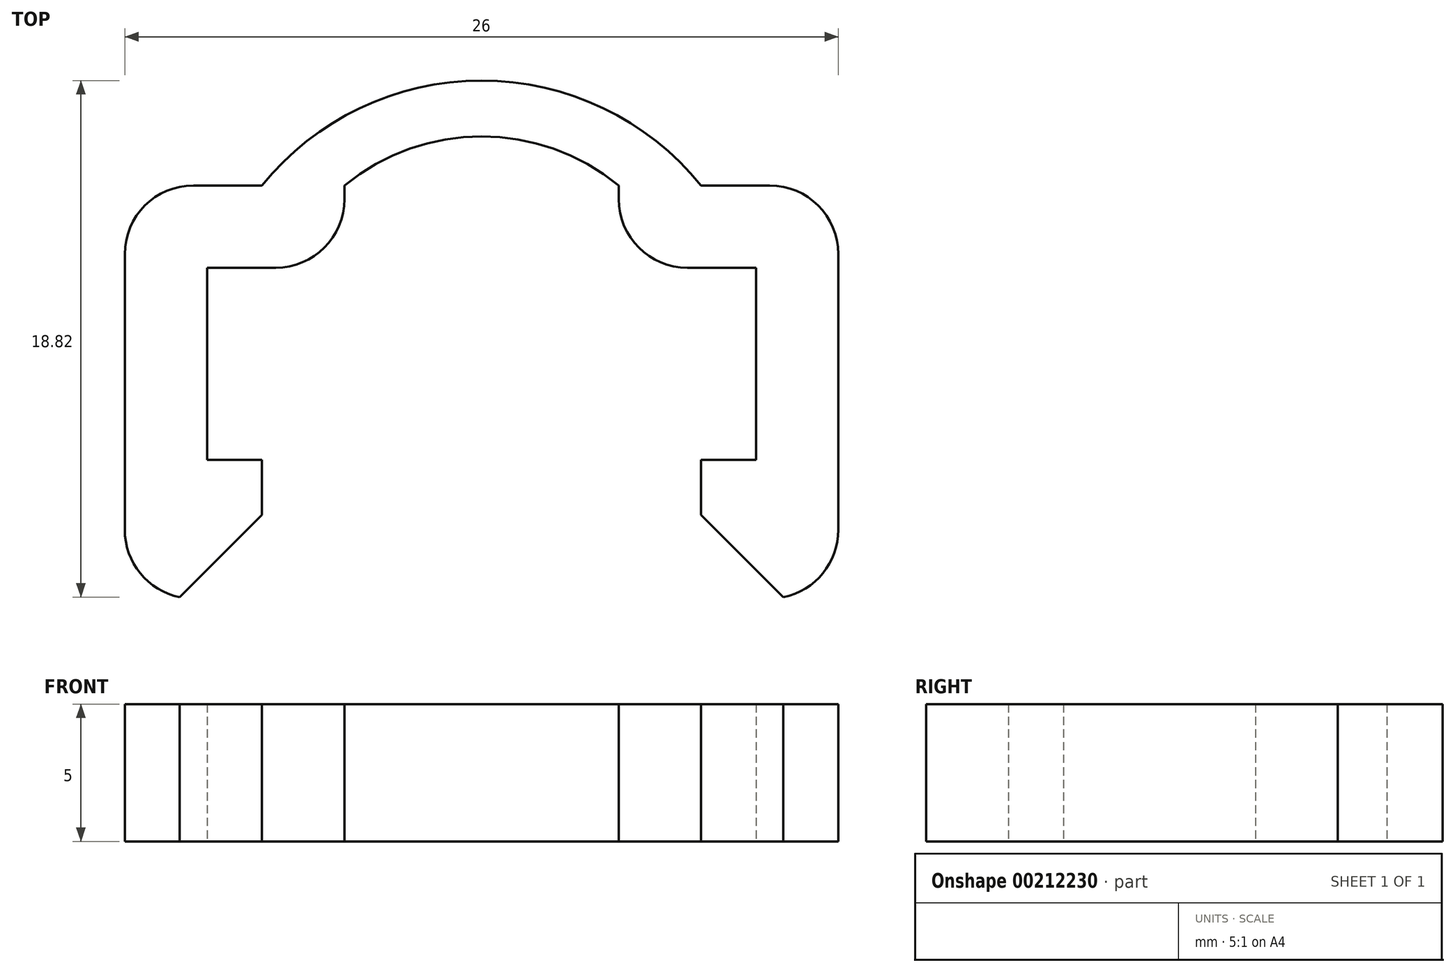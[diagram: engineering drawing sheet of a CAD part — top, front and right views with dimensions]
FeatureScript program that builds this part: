
annotation { "Feature Type Name" : "Feature", "Feature Type Description" : "" }
export const myFeature = defineFeature(function(context is Context, id is Id, definition is map)
    precondition{}
    {
        {
            var Q0;
            Q0=qCreatedBy(makeId("Top.planeOp"),FACE);
            var sketch = newSketch(context, id + "F0", { "sketchPlane" : qUnion([Q0])});
            skLineSegment(sketch, "E0.bottom", {"start": v(-13, 0) * mm, "end": v(-10, 0) * mm});
            skLineSegment(sketch, "E0.top", {"start": v(-13, 15) * mm, "end": v(-10, 15) * mm});
            skLineSegment(sketch, "E0.left", {"start": v(-13, 0) * mm, "end": v(-13, 15) * mm});
            skLineSegment(sketch, "E0.right", {"start": v(-10, 5) * mm, "end": v(-10, 12) * mm});
            skLineSegment(sketch, "E1.top", {"start": v(-10, 12) * mm, "end": v(-5, 12) * mm});
            skLineSegment(sketch, "E1.left", {"start": v(-13, 12) * mm, "end": v(-13, 15) * mm});
            skLineSegment(sketch, "E2.bottom", {"start": v(-10, 5) * mm, "end": v(-8, 5) * mm});
            skLineSegment(sketch, "E2.right", {"start": v(-8, 5) * mm, "end": v(-8, 0) * mm});
            skLineSegment(sketch, "E3", {"start": v(-5, 15) * mm, "end": v(-5, 12) * mm});
            skLineSegment(sketch, "E4", {"start": v(-10, 0) * mm, "end": v(-8, 0) * mm});
            skLineSegment(sketch, "E5.MirrorCS", {"start": v(5, 15) * mm, "end": v(5, 12) * mm});
            skLineSegment(sketch, "E6.MirrorCS", {"start": v(10, 12) * mm, "end": v(5, 12) * mm});
            skLineSegment(sketch, "E7.MirrorCS", {"start": v(10, 5) * mm, "end": v(10, 12) * mm});
            skLineSegment(sketch, "E8.MirrorCS", {"start": v(10, 5) * mm, "end": v(8, 5) * mm});
            skLineSegment(sketch, "E9.MirrorCS", {"start": v(8, 5) * mm, "end": v(8, 0) * mm});
            skLineSegment(sketch, "E10.MirrorCS", {"start": v(10, 0) * mm, "end": v(8, 0) * mm});
            skLineSegment(sketch, "E11.MirrorCS", {"start": v(13, 0) * mm, "end": v(10, 0) * mm});
            skLineSegment(sketch, "E12.MirrorCS", {"start": v(13, 0) * mm, "end": v(13, 15) * mm});
            skLineSegment(sketch, "E13.MirrorCS", {"start": v(13, 15) * mm, "end": v(10, 15) * mm});
            skLineSegment(sketch, "E14", {"start": v(-18.88, 19) * mm, "end": v(22.75, 19) * mm, "construction": true});
            skPoint(sketch, "E15.MirrorCS.end.orphan", {"position": v(5, 15) * mm});
            skPoint(sketch, "E16.MirrorCS.end.orphan", {"position": v(10, 15) * mm});
            skLineSegment(sketch, "E17", {"start": v(-10, 15) * mm, "end": v(-8, 15) * mm});
            skLineSegment(sketch, "E18.MirrorCS", {"start": v(10, 15) * mm, "end": v(8, 15) * mm});
            skArc(sketch, "E19", {"start": v(8, 15) * mm, "mid": v(0, 18.82) * mm, "end": v(-8, 15) * mm});
            skArc(sketch, "E20", {"start": v(5, 15) * mm, "mid": v(0, 16.79) * mm, "end": v(-5, 15) * mm});
            skSolve(sketch);
        }
        {
            var Q0;
            Q0=makeQuery(id+"F0.imprint","IMPRINT",FACE,{"disambiguationData":[TD([[makeQuery(id+"F0.imprint","IMPRINT",EDGE,{"derivedFrom":sQuery(id+"F0.wireOp",EDGE,"E0.bottom")}),1.0]])]});
            var Q1;
            Q1=makeQuery(id+"F0.imprint","IMPRINT",FACE,{"disambiguationData":[TD([[makeQuery(id+"F0.imprint","IMPRINT",EDGE,{"derivedFrom":sQuery(id+"F0.wireOp",EDGE,"CjIfAklJ-aNhK-wlnI-JUxm-dVU2cnHGPbYa")}),-1.0]])]});
            var Q2;
            {var subQ1=sQuery(id+"F0.wireOp",EDGE,"E5.MirrorCS");Q2=makeQuery(id+"F0.imprint","IMPRINT",FACE,{"disambiguationData":[TD([[makeQuery(id+"F0.imprint","IMPRINT",EDGE,{"derivedFrom":subQ1}),1.0]])]});}
            extrude(context, id + "F1", {"entities" : qUnion([Q0, Q1, Q2]), "depth" : 5 * mm});
        }
        {
            var Q0;
            Q0=makeQuery(id+"F1.opExtrude","SWEPT_EDGE",EDGE,{"disambiguationData":[OSD([sQuery(id+"F0.wireOp",EDGE,"E2.right"),sQuery(id+"F0.wireOp",EDGE,"E4")])]});
            var Q1;
            Q1=makeQuery(id+"F1.opExtrude","SWEPT_EDGE",EDGE,{"disambiguationData":[OSD([sQuery(id+"F0.wireOp",EDGE,"E9.MirrorCS"),sQuery(id+"F0.wireOp",EDGE,"E10.MirrorCS")])]});
            chamfer(context, id + "F2", {"entities" : qUnion([Q0, Q1]), "width" : 3 * mm, "tangentPropagation" : true});
        }
        {
            var Q0;
            Q0=makeQuery(id+"F1.opExtrude","SWEPT_EDGE",EDGE,{"disambiguationData":[OSD([sQuery(id+"F0.wireOp",EDGE,"E0.bottom"),sQuery(id+"F0.wireOp",EDGE,"E0.left")])]});
            var Q1;
            Q1=makeQuery(id+"F1.opExtrude","SWEPT_EDGE",EDGE,{"disambiguationData":[OSD([sQuery(id+"F0.wireOp",EDGE,"E0.top"),sQuery(id+"F0.wireOp",EDGE,"E1.left")])]});
            var Q2;
            Q2=makeQuery(id+"F1.opExtrude","SWEPT_EDGE",EDGE,{"disambiguationData":[OSD([sQuery(id+"F0.wireOp",EDGE,"E12.MirrorCS"),sQuery(id+"F0.wireOp",EDGE,"E13.MirrorCS")])]});
            var Q3;
            Q3=makeQuery(id+"F1.opExtrude","SWEPT_EDGE",EDGE,{"disambiguationData":[OSD([sQuery(id+"F0.wireOp",EDGE,"E11.MirrorCS"),sQuery(id+"F0.wireOp",EDGE,"E12.MirrorCS")])]});
            var Q4;
            Q4=makeQuery(id+"F1.opExtrude","SWEPT_EDGE",EDGE,{"disambiguationData":[OSD([sQuery(id+"F0.wireOp",EDGE,"E1.top"),sQuery(id+"F0.wireOp",EDGE,"E3")])]});
            var Q5;
            Q5=makeQuery(id+"F1.opExtrude","SWEPT_EDGE",EDGE,{"disambiguationData":[OSD([sQuery(id+"F0.wireOp",EDGE,"E5.MirrorCS"),sQuery(id+"F0.wireOp",EDGE,"E6.MirrorCS")])]});
            fillet(context, id + "F3", {"entities" : qUnion([Q0, Q1, Q2, Q3, Q4, Q5]), "radius" : 2.5 * mm, "tangentPropagation" : true, "allowEdgeOverflow" : false});
        }
    });
